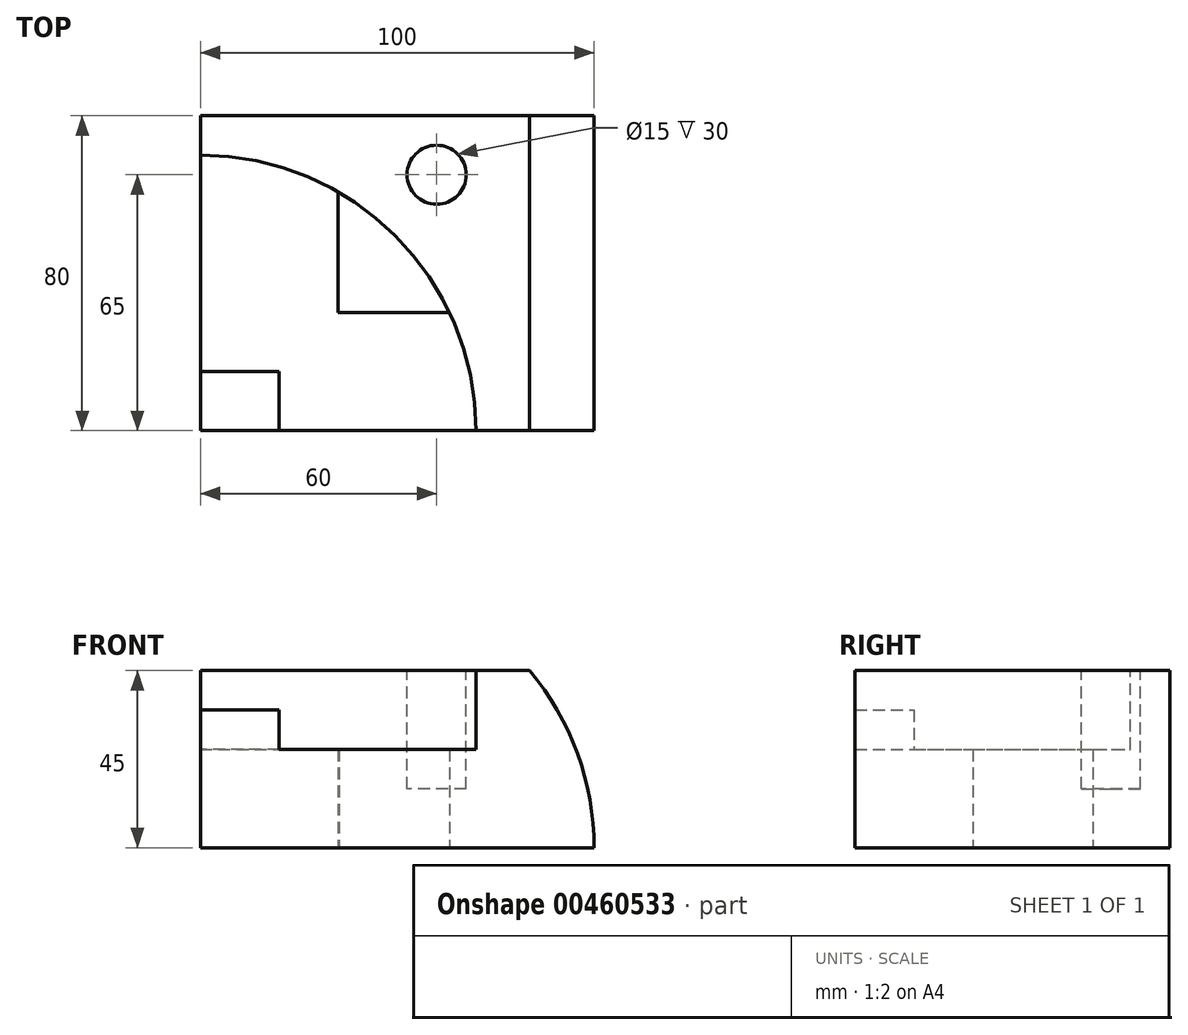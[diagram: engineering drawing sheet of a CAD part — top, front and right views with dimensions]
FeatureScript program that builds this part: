
annotation { "Feature Type Name" : "Feature", "Feature Type Description" : "" }
export const myFeature = defineFeature(function(context is Context, id is Id, definition is map)
    precondition{}
    {
        {
            var Q0;
            Q0=qCreatedBy(makeId("Front.planeOp"),FACE);
            var sketch = newSketch(context, id + "F0", { "sketchPlane" : qUnion([Q0])});
            skLineSegment(sketch, "E0.bottom", {"start": v(0, 0) * mm, "end": v(-100, 0) * mm});
            skLineSegment(sketch, "E0.top", {"start": v(0, 45) * mm, "end": v(-100, 45) * mm});
            skLineSegment(sketch, "E0.left", {"start": v(0, 0) * mm, "end": v(0, 45) * mm});
            skLineSegment(sketch, "E0.right", {"start": v(-100, 0) * mm, "end": v(-100, 45) * mm});
            skSolve(sketch);
        }
        {
            var Q0;
            Q0=makeQuery(id+"F0.imprint","IMPRINT",FACE,{"disambiguationData":[TD([[makeQuery(id+"F0.imprint","IMPRINT",EDGE,{"derivedFrom":sQuery(id+"F0.wireOp",EDGE,"E0.bottom")}),-1.0]])]});
            extrude(context, id + "F1", {"entities" : qUnion([Q0]), "depth" : 80 * mm});
        }
        {
            var Q0;
            Q0=makeQuery(id+"F1.opExtrude","CAP_FACE",FACE,{"disambiguationData":[OSD([sQuery(id+"F0.wireOp",EDGE,"E0.bottom"),sQuery(id+"F0.wireOp",EDGE,"E0.top"),sQuery(id+"F0.wireOp",EDGE,"E0.left"),sQuery(id+"F0.wireOp",EDGE,"E0.right")])],"isStart":false});
            var sketch = newSketch(context, id + "F2", { "sketchPlane" : qUnion([Q0])});
            skLineSegment(sketch, "E1", {"start": v(0, 0) * mm, "end": v(-70, 0) * mm});
            skCircle(sketch, "E2", {"center": v(-70, 0) * mm, "radius": 70 * mm});
            skSolve(sketch);
        }
        {
            var Q0;
            {var subQ1=makeQuery(id+"F1.opExtrude","CAP_EDGE",EDGE,{"disambiguationData":[OSD([sQuery(id+"F0.wireOp",EDGE,"E0.left")])],"isStart":false});Q0=makeQuery(id+"F2.imprint","IMPRINT",FACE,{"disambiguationData":[TD([[makeQuery(id+"F2.imprint","IMPRINT",EDGE,{"derivedFrom":subQ1}),1.0]])]});}
            extrude(context, id + "F3", {"entities" : qUnion([Q0]), "operationType" : NewBodyOperationType.REMOVE, "endBound" : BoundingType.UP_TO_NEXT, "oppositeDirection" : true, "depth" : 25 * mm});
        }
        {
            var Q0;
            Q0=makeQuery(id+"F1.opExtrude","SWEPT_FACE",FACE,{"disambiguationData":[OSD([sQuery(id+"F0.wireOp",EDGE,"E0.top")])]});
            var sketch = newSketch(context, id + "F4", { "sketchPlane" : qUnion([Q0])});
            skCircle(sketch, "E3", {"center": v(-100, -80) * mm, "radius": 70 * mm});
            skSolve(sketch);
        }
        {
            var Q0;
            {var subQ0=sQuery(id+"F4.wireOp",EDGE,"E3");var subQ1=sQuery(id+"F0.wireOp",EDGE,"E0.top");var subQ4=makeQuery(id+"F1.opExtrude","CAP_EDGE",EDGE,{"disambiguationData":[OSD([subQ1])],"isStart":false});var subQ5=makeQuery(id+"F4.imprint","INTERSECT",VERTEX,{"derivedFrom":[subQ4,subQ0]});Q0=makeQuery(id+"F4.imprint","IMPRINT",FACE,{"disambiguationData":[TD([[makeQuery(id+"F4.imprint","IMPRINT",EDGE,{"disambiguationData":[TD([[subQ5,-1.0]])],"derivedFrom":subQ0}),1.0]])]});}
            extrude(context, id + "F5", {"entities" : qUnion([Q0]), "operationType" : NewBodyOperationType.REMOVE, "oppositeDirection" : true, "depth" : 20 * mm});
        }
        {
            var Q0;
            Q0=makeQuery(id+"F5.boolean.opBoolean","COPY",FACE,{"derivedFrom":makeQuery(id+"F5.opExtrude","CAP_FACE",FACE,{"disambiguationData":[OSD([sQuery(id+"F0.wireOp",EDGE,"E0.top"),sQuery(id+"F0.wireOp",EDGE,"E0.right"),sQuery(id+"F4.wireOp",EDGE,"E3")])],"isStart":false})});
            var sketch = newSketch(context, id + "F6", { "sketchPlane" : qUnion([Q0])});
            skLineSegment(sketch, "E4.bottom", {"start": v(-100, -80) * mm, "end": v(-80, -80) * mm});
            skLineSegment(sketch, "E4.top", {"start": v(-100, -65) * mm, "end": v(-80, -65) * mm});
            skLineSegment(sketch, "E4.left", {"start": v(-100, -80) * mm, "end": v(-100, -65) * mm});
            skLineSegment(sketch, "E4.right", {"start": v(-80, -80) * mm, "end": v(-80, -65) * mm});
            skSolve(sketch);
        }
        {
            var Q0;
            Q0=makeQuery(id+"F6.imprint","IMPRINT",FACE,{"disambiguationData":[TD([[makeQuery(id+"F6.imprint","IMPRINT",EDGE,{"derivedFrom":sQuery(id+"F6.wireOp",EDGE,"E4.bottom")}),-1.0]])]});
            extrude(context, id + "F7", {"entities" : qUnion([Q0]), "operationType" : NewBodyOperationType.ADD, "depth" : 10 * mm});
        }
        {
            var Q0;
            Q0=makeQuery(id+"F1.opExtrude","SWEPT_FACE",FACE,{"disambiguationData":[OSD([sQuery(id+"F0.wireOp",EDGE,"E0.top")])]});
            var sketch = newSketch(context, id + "F8", { "sketchPlane" : qUnion([Q0])});
            skPoint(sketch, "E5", {"position": v(-40, -15) * mm});
            skCircle(sketch, "E6", {"center": v(-40, -15) * mm, "radius": 7.5 * mm});
            skSolve(sketch);
        }
        {
            var Q0;
            Q0=makeQuery(id+"F8.imprint","IMPRINT",FACE,{"disambiguationData":[TD([[makeQuery(id+"F8.imprint","IMPRINT",EDGE,{"derivedFrom":sQuery(id+"F8.wireOp",EDGE,"E6")}),1.0]])]});
            extrude(context, id + "F9", {"entities" : qUnion([Q0]), "operationType" : NewBodyOperationType.REMOVE, "oppositeDirection" : true, "depth" : 30 * mm});
        }
        {
            var Q0;
            Q0=makeQuery(id+"F1.opExtrude","SWEPT_FACE",FACE,{"disambiguationData":[OSD([sQuery(id+"F0.wireOp",EDGE,"E0.bottom")])]});
            var sketch = newSketch(context, id + "F10", { "sketchPlane" : qUnion([Q0])});
            skLineSegment(sketch, "E7.bottom", {"start": v(-65, 50) * mm, "end": v(-36.75, 50) * mm});
            skLineSegment(sketch, "E7.top", {"start": v(-65, 19.5) * mm, "end": v(-36.75, 19.5) * mm});
            skLineSegment(sketch, "E7.left", {"start": v(-65, 50) * mm, "end": v(-65, 19.5) * mm});
            skLineSegment(sketch, "E7.right", {"start": v(-36.75, 50) * mm, "end": v(-36.75, 19.5) * mm});
            skCircle(sketch, "E8", {"center": v(-100, 80) * mm, "radius": 70 * mm});
            skSolve(sketch);
        }
        {
            var Q0;
            {var subQ0=sQuery(id+"F10.wireOp",EDGE,"E7.left");Q0=makeQuery(id+"F10.imprint","IMPRINT",FACE,{"disambiguationData":[TD([[makeQuery(id+"F10.imprint","IMPRINT",EDGE,{"derivedFrom":subQ0}),1.0]])]});}
            extrude(context, id + "F11", {"entities" : qUnion([Q0]), "operationType" : NewBodyOperationType.REMOVE, "oppositeDirection" : true, "depth" : 25 * mm});
        }
    });
